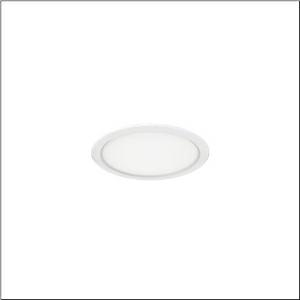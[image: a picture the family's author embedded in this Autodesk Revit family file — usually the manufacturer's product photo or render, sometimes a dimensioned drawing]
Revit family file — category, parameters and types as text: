
# Revit family: lunis_41_eco_51ds107d43a
name_source: partatom
category: Lighting Fixtures
units: mm (PartAtom-declared; Revit-internal decimal feet)

## family parameters
Cut with Voids When Loaded = No
Host = Face
Light Source = No
Part Type = Normal
Room Calculation Point = No
Round Connector Dimension = Use Diameter
Shared = No

## types (1)
- Lunis 41 ECO (1 x LED, 1460 lm, 14 W, 4000K)
    Apparent Load = 14 VA
    CIE Flux Codes = 47 80 97 100 100
    Color Rendering = 80
    Color Temperature = 4000K
    Default Elevation = 1800 mm
    Description = Lunis 41,  ECO, downlight, light emission: direct distribution, LED rated luminous flux: 1.460lm, light colour: 840, control gear: ECG, mains connection: 230V, AC, 50/60Hz, housing, round, of aluminium, coated, traffic white (RAL 9016), diameter: 166mm, recess depth: 54mm, protection rating (complete): IP20, insulation class (complete): insulation class II (safety insulation), certification: CE, permissible ambient temperature for indoor applications: -20..+40°C, packaging unit: 1 piece
    Height = 0 mm  [stored 0 ft]
    Lamp = 1 x LED
    Lamp Light Flux = 1460 lm
    Lamp Power = 14 W
    Lamp count = 1
    Length = 165 mm
    Luminous efficacy = 104 lm/W
    Manufacturer = Siteco
    ModVariant = No
    Model = 51DS107D43A
    Mounting Place = Ceiling
    Mounting Type = Recessed
    Number of Poles = 1
    OnlyDefault = Yes
    Power Factor = 1
    Product Name = Lunis 41 ECO
    Product group = downlight | ceiling recessed
    ProductGroupID = 402
    Protection Class = Protection class II
    Protection Degree = IP 20
    RLX_Detail_Level = 1
    RlxData = <blob elided: 25709 chars, md5=2bebce04>
    Socket = socket
    Standby Power = 0 W
    System Light Flux = 1460 lm
    System Power = 14 W
    Type Comments = Product without accessories
    Type Image = l_1007041.jpg
    URL = http://relux.com
    VarID = ---
    Voltage = 0 V
    Weight = 0.00 kg
    Width = 0 mm  [stored 0 ft]

note: [stored X ft] marks values corroborated as IEEE doubles in the binary element streams (Revit-internal decimal feet)

## geometry (parser evidence)
native form markers: Blend x4, Sweep x12
no freeform markers — native parametric forms only
